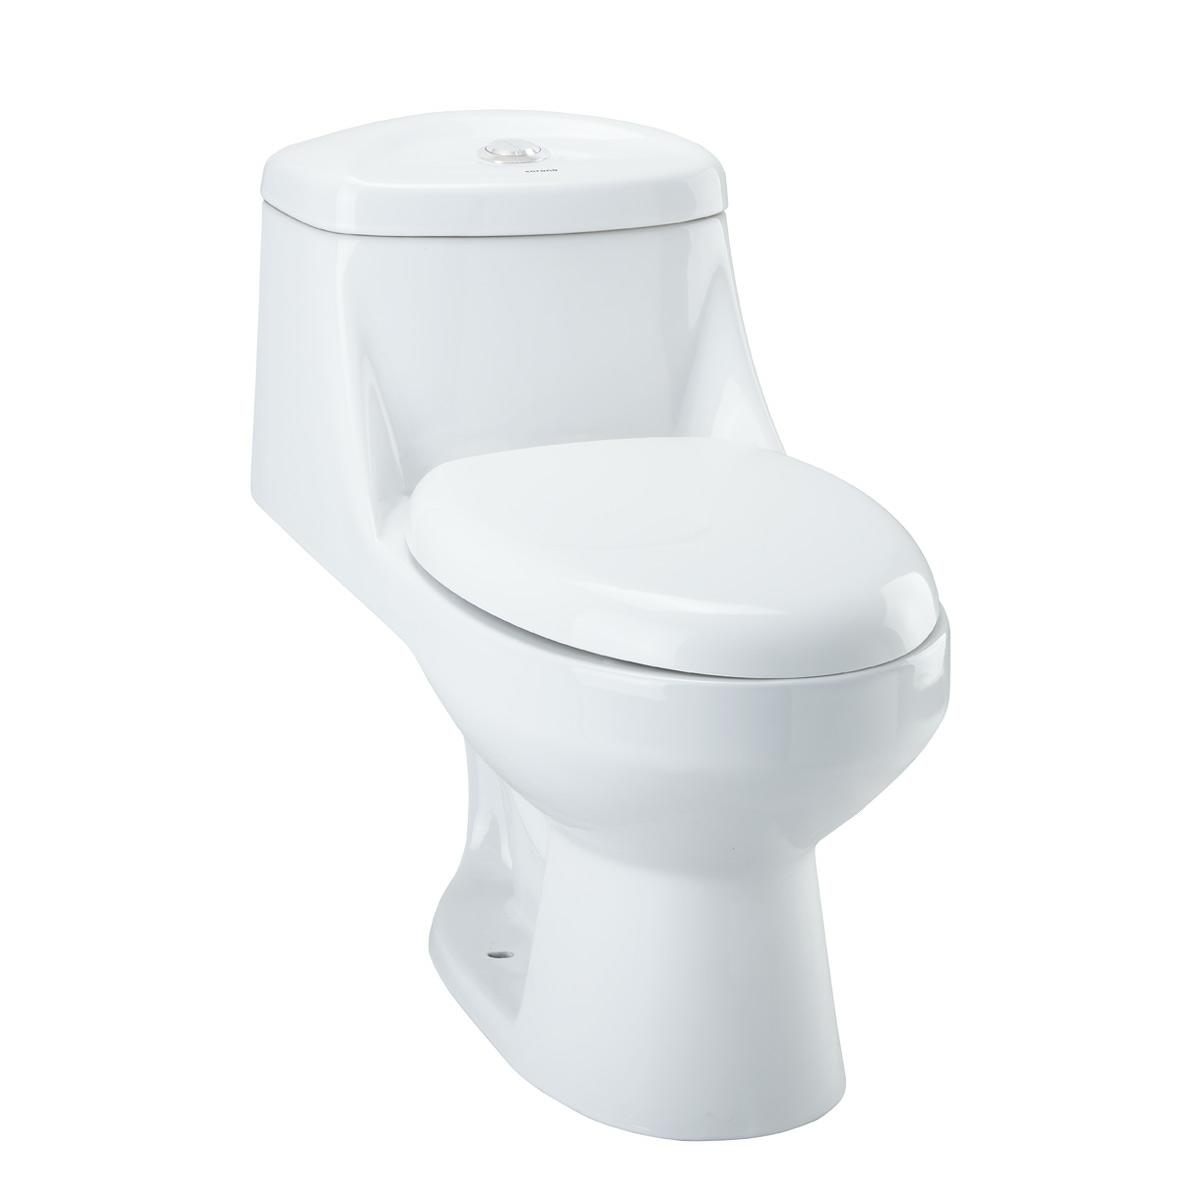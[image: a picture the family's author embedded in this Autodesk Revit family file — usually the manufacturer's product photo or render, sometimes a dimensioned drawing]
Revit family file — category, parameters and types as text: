
# Revit family: CCMX-CORONA_OPORTO
name_source: partatom
category: Plumbing Fixtures
units: mm (PartAtom-declared; Revit-internal decimal feet)

## family parameters
Always vertical = Yes
Cut with Voids When Loaded = No
OmniClass Number = 23.45.00.00
OmniClass Title = Sanitary, Laundry, and Cleaning Equipment
Part Type = Normal
Room Calculation Point = No
Round Connector Dimension = Use Diameter
Shared = No
Work Plane-Based = No

## types (1)
- CCMX-CORONA_OPORTO
    Assembly Code = D2010.60
    Consumo = Consumo de agua 4 y 6 litros, accionamiento de botón Dual Flush
    Description = Diseño cómodo e ideal para espacios pequeños. Consumo de agua 4 y 6 litros, accionamiento de botón Dual Flush. Capacidad de evacuación 500 gramos. Incluye asiento de cierre suave.
    Dimensiones = https://coronamexico.com
    Ficha Tecnica = https://coronamexico.com
    Garantia de Producto = 20 años en porcelana sanitaria
    Keynote = 224113
    Manufacturer = CORONA
    Model = One Piece Oporto
    Type Image = ONE PIECE OPORTO.jpg
    URL = https://coronamexico.com

## geometry (parser evidence)
native form markers: Sweep x3
no freeform markers — native parametric forms only
